# Revit family: Montageschiene 45- 45-2,0  6m, V4A
name_source: partatom
category: HLS-Bauteile
revit_build: Autodesk Revit 2017 (Build: 20190507_1515(x64)
units: mm (PartAtom-declared; Revit-internal decimal feet)

## family parameters
Arbeitsebenenbasiert = Ja
Beim Laden mit Abzugskörper schneiden = Nein
Bemaßung runder Anschluss = Durchmesser verwenden
Gemeinsam genutzt = Ja
Immer vertikal = Nein
Raumberechnungspunkt = Nein
Teiletyp = Normal

## types (1)
- C-Profil 45- 45-2,0  L=6000, V4A
    Abmessung = 45/45/2.0 mm
    Artikelnummer = 080015501
    Breite = 45 mm  [stored 0.147638 ft]
    Bund = 240 m
    EAN = 4250928456793
    Fabrikat = MEFA
    Firma = MEFA Befestigungs- und Montagesysteme GmbH
    Fläche (schwächster Profilquerschnitt) = 0 m²
    Gewicht = 2,50 kg
    Höhe = 45 mm
    Kurztext1 = Montageschiene C-Profil V4A
    Kurztext2 = 45 / 45 / 2 mm L= 6 m
    Langloch = 14 x 45 mm
    Lochdurchmesser = 14 mm
    Länge = 6000 mm  [stored 19.685 ft]
    Material = Edelstahl
    Schlitzbreite = 22 mm
    Schwerpunktabstand eo = 2,27 cm
    Schwerpunktabstand eu = 2,22 cm
    Schwerpunktabstand ez = 2,25 cm
    Streckgrenze = 240 N/mm²
    Stärke = 2 mm  [stored 0.00656168 ft]
    Trägheitsradius iy = 1,62 cm
    Trägheitsradius iz = 1,91 cm
    Vorgabe-Ansicht = 1219 mm
    Widerstandsmoment Wy = 3,28 cm³
    Widerstandsmoment Wz = 4,61 cm³
    vpe = 30

note: [stored X ft] marks values corroborated as IEEE doubles in the binary element streams (Revit-internal decimal feet)
